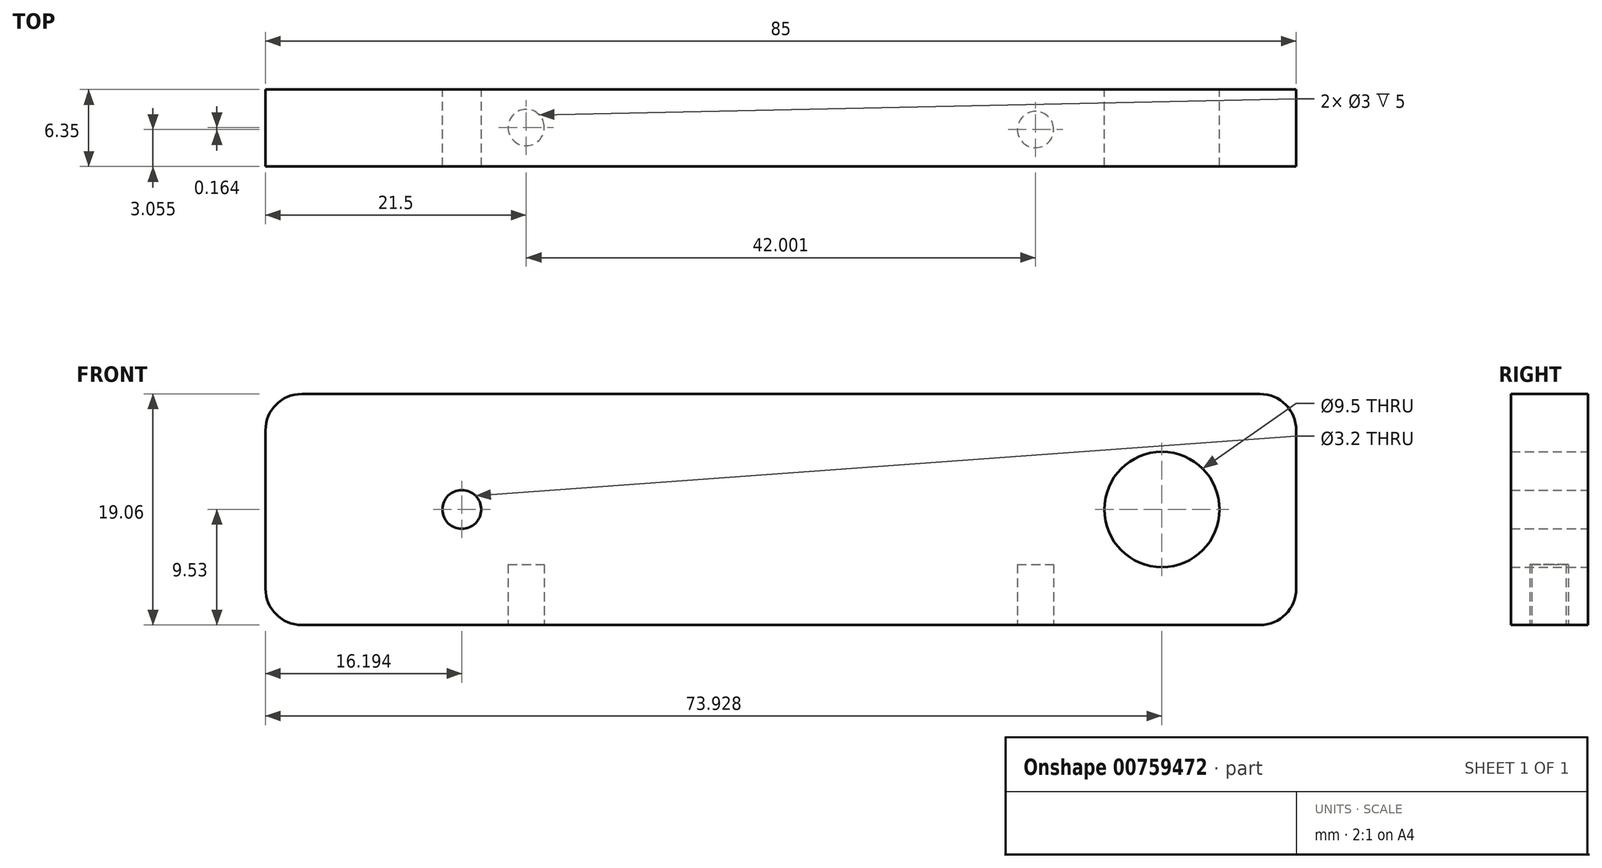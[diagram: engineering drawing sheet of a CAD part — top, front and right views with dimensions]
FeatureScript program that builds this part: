
annotation { "Feature Type Name" : "Feature", "Feature Type Description" : "" }
export const myFeature = defineFeature(function(context is Context, id is Id, definition is map)
    precondition{}
    {
        {
            var Q0;
            Q0=qCreatedBy(makeId("Front.planeOp"),FACE);
            var sketch = newSketch(context, id + "F0", { "sketchPlane" : qUnion([Q0])});
            skLineSegment(sketch, "E0.bottom", {"start": v(-39.5, 9.53) * mm, "end": v(39.5, 9.53) * mm});
            skLineSegment(sketch, "E0.top", {"start": v(-39.5, -9.53) * mm, "end": v(39.5, -9.53) * mm});
            skLineSegment(sketch, "E0.left", {"start": v(-42.5, 6.53) * mm, "end": v(-42.5, -6.53) * mm});
            skLineSegment(sketch, "E0.right", {"start": v(42.5, 6.53) * mm, "end": v(42.5, -6.53) * mm});
            skPoint(sketch, "E0.middle", {"position": v(0, 0) * mm});
            skCircle(sketch, "E1", {"center": v(-26.3, 0) * mm, "radius": 1.6 * mm});
            skCircle(sketch, "E2", {"center": v(31.43, 0) * mm, "radius": 4.75 * mm});
            skPoint(sketch, "E3.visualSharp", {"position": v(-42.5, 9.53) * mm});
            skArc(sketch, "E3.filletArc", {"start": v(-39.5, 9.53) * mm, "mid": v(-41.62, 8.65) * mm, "end": v(-42.5, 6.53) * mm});
            skPoint(sketch, "E4.visualSharp", {"position": v(-42.5, -9.53) * mm});
            skArc(sketch, "E4.filletArc", {"start": v(-42.5, -6.53) * mm, "mid": v(-41.62, -8.65) * mm, "end": v(-39.5, -9.52) * mm});
            skPoint(sketch, "E5.visualSharp", {"position": v(42.5, -9.53) * mm});
            skArc(sketch, "E5.filletArc", {"start": v(39.5, -9.53) * mm, "mid": v(41.62, -8.65) * mm, "end": v(42.5, -6.53) * mm});
            skPoint(sketch, "E6.visualSharp", {"position": v(42.5, 9.53) * mm});
            skArc(sketch, "E6.filletArc", {"start": v(42.5, 6.53) * mm, "mid": v(41.62, 8.65) * mm, "end": v(39.5, 9.53) * mm});
            skSolve(sketch);
        }
        {
            var Q0;
            Q0 = qSketchRegion(id + "F0", true);
            var Q1;
            Q1=makeQuery(id+"F0.imprint","IMPRINT",FACE,{"disambiguationData":[TD([[makeQuery(id+"F0.imprint","IMPRINT",EDGE,{"derivedFrom":sQuery(id+"F0.wireOp",EDGE,"E1")}),1.0]])]});
            extrude(context, id + "F1", {"entities" : qUnion([Q0, Q1]), "depth" : 6.35 * mm, "offsetDistance" : 25 * mm});
        }
        {
            var Q0;
            Q0=makeQuery(id+"F1.opExtrude","SWEPT_FACE",FACE,{"disambiguationData":[OSD([sQuery(id+"F0.wireOp",EDGE,"E0.top")])]});
            var sketch = newSketch(context, id + "F2", { "sketchPlane" : qUnion([Q0])});
            skCircle(sketch, "E7.0", {"center": v(-21, 3.13) * mm, "radius": 1.5 * mm});
            skCircle(sketch, "E8.0", {"center": v(21, 3.3) * mm, "radius": 1.5 * mm});
            skSolve(sketch);
        }
        {
            var Q0;
            Q0 = qSketchRegion(id + "F2", true);
            extrude(context, id + "F3", {"entities" : qUnion([Q0]), "operationType" : NewBodyOperationType.REMOVE, "oppositeDirection" : true, "depth" : 5 * mm, "offsetDistance" : 25 * mm});
        }
        {
            var Q0;
            Q0=makeQuery(id+"F0.imprint","IMPRINT",FACE,{"disambiguationData":[TD([[makeQuery(id+"F0.imprint","IMPRINT",EDGE,{"derivedFrom":sQuery(id+"F0.wireOp",EDGE,"E1")}),1.0]])]});
            extrude(context, id + "F4", {"entities" : qUnion([Q0]), "operationType" : NewBodyOperationType.REMOVE, "oppositeDirection" : true, "depth" : 25 * mm, "offsetDistance" : 25 * mm});
        }
        {
            var Q0;
            Q0=makeQuery(id+"F0.imprint","IMPRINT",FACE,{"disambiguationData":[TD([[makeQuery(id+"F0.imprint","IMPRINT",EDGE,{"derivedFrom":sQuery(id+"F0.wireOp",EDGE,"E1")}),1.0]])]});
            extrude(context, id + "F5", {"entities" : qUnion([Q0]), "operationType" : NewBodyOperationType.REMOVE, "depth" : 25 * mm, "offsetDistance" : 25 * mm});
        }
    });
